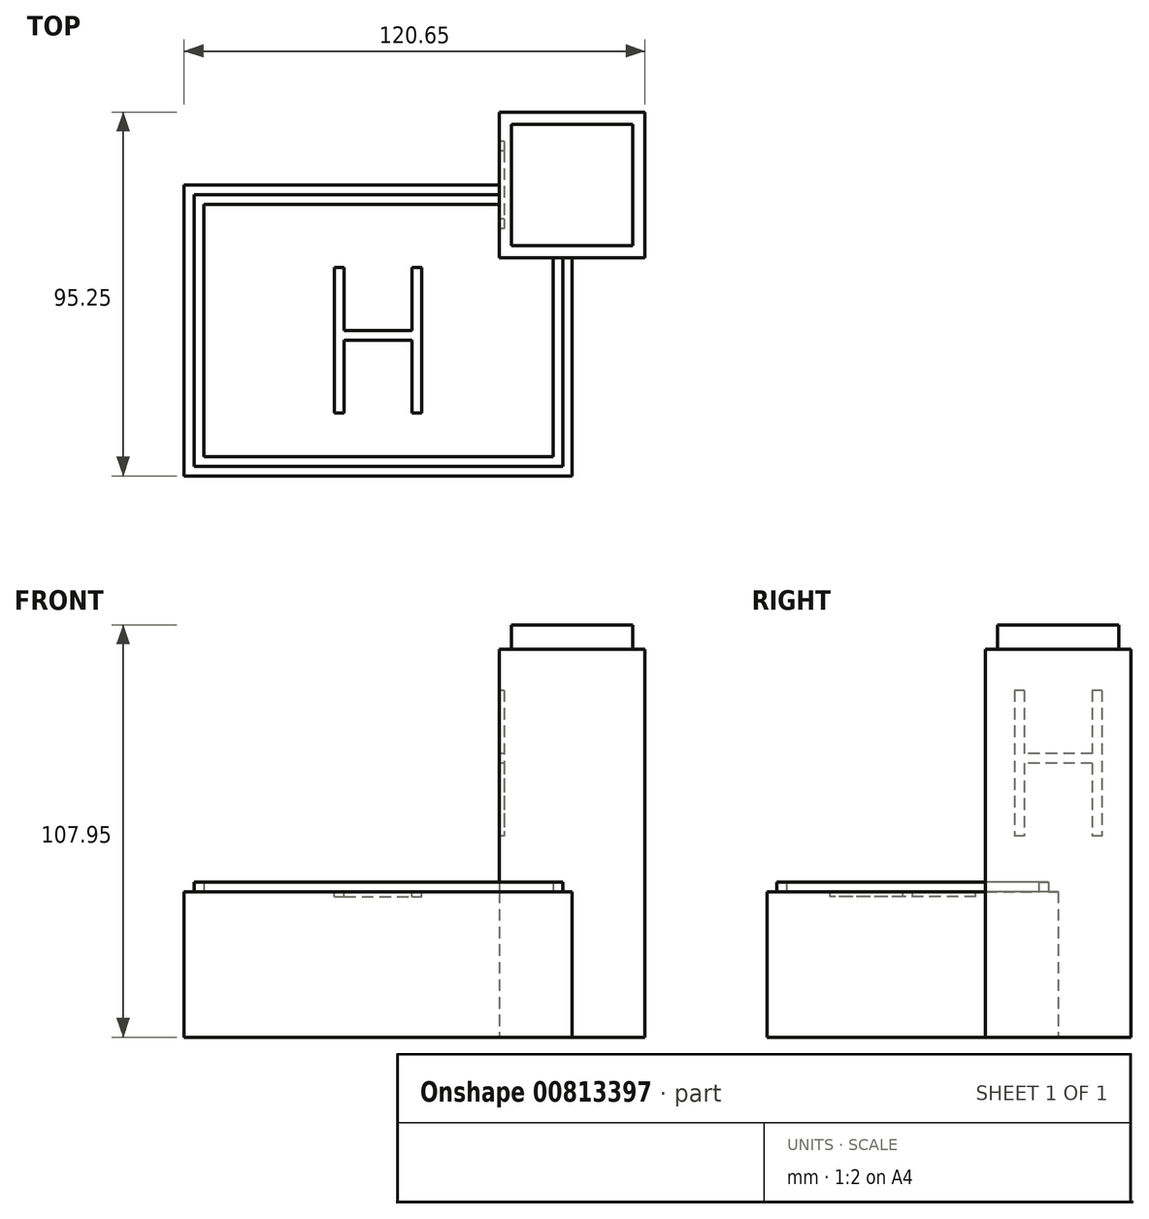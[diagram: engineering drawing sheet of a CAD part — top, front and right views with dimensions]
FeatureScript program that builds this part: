
annotation { "Feature Type Name" : "Feature", "Feature Type Description" : "" }
export const myFeature = defineFeature(function(context is Context, id is Id, definition is map)
    precondition{}
    {
        {
            var Q0;
            Q0=qCreatedBy(makeId("Top.planeOp"),FACE);
            var sketch = newSketch(context, id + "F0", { "sketchPlane" : qUnion([Q0])});
            skLineSegment(sketch, "E0.bottom", {"start": v(-50.8, 38.1) * mm, "end": v(50.8, 38.1) * mm});
            skLineSegment(sketch, "E0.top", {"start": v(-50.8, -38.1) * mm, "end": v(50.8, -38.1) * mm});
            skLineSegment(sketch, "E0.left", {"start": v(-50.8, 38.1) * mm, "end": v(-50.8, -38.1) * mm});
            skLineSegment(sketch, "E0.right", {"start": v(50.8, 38.1) * mm, "end": v(50.8, -38.1) * mm});
            skLineSegment(sketch, "E1.bottom", {"start": v(31.75, 57.15) * mm, "end": v(69.85, 57.15) * mm});
            skLineSegment(sketch, "E1.top", {"start": v(31.75, 19.05) * mm, "end": v(69.85, 19.05) * mm});
            skLineSegment(sketch, "E1.left", {"start": v(31.75, 57.15) * mm, "end": v(31.75, 19.05) * mm});
            skLineSegment(sketch, "E1.right", {"start": v(69.85, 57.15) * mm, "end": v(69.85, 19.05) * mm});
            skSolve(sketch);
        }
        {
            var Q0;
            {var subQ1=sQuery(id+"F0.wireOp",EDGE,"E0.top");Q0=makeQuery(id+"F0.imprint","IMPRINT",FACE,{"disambiguationData":[TD([[makeQuery(id+"F0.imprint","IMPRINT",EDGE,{"derivedFrom":subQ1}),1.0]])]});}
            var Q1;
            {var subQ0=sQuery(id+"F0.wireOp",EDGE,"E0.right");var subQ1=sQuery(id+"F0.wireOp",EDGE,"E0.bottom");var subQ2=makeQuery(id+"F0.imprint","INTERSECT",VERTEX,{"derivedFrom":[subQ1,subQ0]});Q1=makeQuery(id+"F0.imprint","IMPRINT",FACE,{"disambiguationData":[TD([[makeQuery(id+"F0.imprint","IMPRINT",EDGE,{"disambiguationData":[TD([[subQ2,1.0]])],"derivedFrom":subQ1}),-1.0]])]});}
            extrude(context, id + "F1", {"entities" : qUnion([Q0, Q1]), "depth" : 38.1 * mm, "offsetDistance" : 25.4 * mm});
        }
        {
            var Q0;
            {var subQ6=sQuery(id+"F0.wireOp",EDGE,"E1.bottom");Q0=makeQuery(id+"F0.imprint","IMPRINT",FACE,{"disambiguationData":[TD([[makeQuery(id+"F0.imprint","IMPRINT",EDGE,{"derivedFrom":subQ6}),-1.0]])]});}
            var Q1;
            {var subQ0=sQuery(id+"F0.wireOp",EDGE,"E0.right");var subQ1=sQuery(id+"F0.wireOp",EDGE,"E0.bottom");var subQ2=makeQuery(id+"F0.imprint","INTERSECT",VERTEX,{"derivedFrom":[subQ1,subQ0]});Q1=makeQuery(id+"F0.imprint","IMPRINT",FACE,{"disambiguationData":[TD([[makeQuery(id+"F0.imprint","IMPRINT",EDGE,{"disambiguationData":[TD([[subQ2,1.0]])],"derivedFrom":subQ1}),-1.0]])]});}
            extrude(context, id + "F2", {"entities" : qUnion([Q0, Q1]), "operationType" : NewBodyOperationType.ADD, "depth" : 101.6 * mm, "offsetDistance" : 25.4 * mm});
        }
        {
            var Q0;
            Q0=makeQuery(id+"F2.opExtrude","CAP_FACE",FACE,{"disambiguationData":[OSD([sQuery(id+"F0.wireOp",EDGE,"E1.bottom"),sQuery(id+"F0.wireOp",EDGE,"E1.top"),sQuery(id+"F0.wireOp",EDGE,"E1.left"),sQuery(id+"F0.wireOp",EDGE,"E1.right")])],"isStart":false});
            var sketch = newSketch(context, id + "F3", { "sketchPlane" : qUnion([Q0])});
            skLineSegment(sketch, "E2.bottom", {"start": v(34.93, 53.97) * mm, "end": v(66.68, 53.97) * mm});
            skLineSegment(sketch, "E2.top", {"start": v(34.93, 22.22) * mm, "end": v(66.68, 22.22) * mm});
            skLineSegment(sketch, "E2.left", {"start": v(34.93, 53.97) * mm, "end": v(34.93, 22.22) * mm});
            skLineSegment(sketch, "E2.right", {"start": v(66.68, 53.97) * mm, "end": v(66.68, 22.22) * mm});
            skSolve(sketch);
        }
        {
            var Q0;
            Q0=makeQuery(id+"F3.imprint","IMPRINT",FACE,{"disambiguationData":[TD([[makeQuery(id+"F3.imprint","IMPRINT",EDGE,{"derivedFrom":sQuery(id+"F3.wireOp",EDGE,"E2.bottom")}),-1.0]])]});
            extrude(context, id + "F4", {"entities" : qUnion([Q0]), "operationType" : NewBodyOperationType.ADD, "depth" : 6.35 * mm, "offsetDistance" : 25.4 * mm});
        }
        {
            var Q0;
            Q0=makeQuery(id+"F1.opExtrude","CAP_FACE",FACE,{"disambiguationData":[OSD([sQuery(id+"F0.wireOp",EDGE,"E0.bottom"),sQuery(id+"F0.wireOp",EDGE,"E0.top"),sQuery(id+"F0.wireOp",EDGE,"E0.left"),sQuery(id+"F0.wireOp",EDGE,"E0.right")])],"isStart":false});
            var sketch = newSketch(context, id + "F5", { "sketchPlane" : qUnion([Q0])});
            skLineSegment(sketch, "E3.bottom", {"start": v(-11.43, 16.51) * mm, "end": v(-8.9, 16.51) * mm});
            skLineSegment(sketch, "E3.top", {"start": v(-11.43, -21.59) * mm, "end": v(-8.9, -21.59) * mm});
            skLineSegment(sketch, "E3.left", {"start": v(-11.43, 16.51) * mm, "end": v(-11.43, -21.59) * mm});
            skLineSegment(sketch, "E3.right", {"start": v(-8.9, 16.51) * mm, "end": v(-8.9, -21.6) * mm});
            skLineSegment(sketch, "E4.bottom", {"start": v(8.89, 16.51) * mm, "end": v(11.43, 16.51) * mm});
            skLineSegment(sketch, "E4.top", {"start": v(8.89, -21.59) * mm, "end": v(11.43, -21.59) * mm});
            skLineSegment(sketch, "E4.left", {"start": v(8.89, 16.51) * mm, "end": v(8.89, -21.59) * mm});
            skLineSegment(sketch, "E4.right", {"start": v(11.43, 16.51) * mm, "end": v(11.43, -21.59) * mm});
            skLineSegment(sketch, "E5.bottom", {"start": v(-8.9, 0) * mm, "end": v(8.89, 0) * mm});
            skLineSegment(sketch, "E5.top", {"start": v(-8.9, -2.54) * mm, "end": v(8.89, -2.54) * mm});
            skLineSegment(sketch, "E5.left", {"start": v(-8.9, 0) * mm, "end": v(-8.9, -2.54) * mm});
            skLineSegment(sketch, "E5.right", {"start": v(8.89, 0) * mm, "end": v(8.89, -2.54) * mm});
            skPoint(sketch, "E6.centerSnap0", {"position": v(0, -2.54) * mm});
            skCircle(sketch, "E7", {"center": v(0, -2.54) * mm, "radius": 22.22 * mm});
            skCircle(sketch, "E8", {"center": v(0, -2.54) * mm, "radius": 23.42 * mm});
            skLineSegment(sketch, "E9", {"start": v(-23.42, -2.76) * mm, "end": v(-22.21, -2.76) * mm, "construction": true});
            skSolve(sketch);
        }
        {
            var Q0;
            Q0=makeQuery(id+"F5.imprint","IMPRINT",FACE,{"disambiguationData":[TD([[makeQuery(id+"F5.imprint","IMPRINT",EDGE,{"derivedFrom":sQuery(id+"F5.wireOp",EDGE,"E5.bottom")}),-1.0]])]});
            var Q1;
            {var subQ1=sQuery(id+"F5.wireOp",EDGE,"E3.bottom");Q1=makeQuery(id+"F5.imprint","IMPRINT",FACE,{"disambiguationData":[TD([[makeQuery(id+"F5.imprint","IMPRINT",EDGE,{"derivedFrom":subQ1}),-1.0]])]});}
            var Q2;
            {var subQ3=sQuery(id+"F5.wireOp",EDGE,"E4.bottom");Q2=makeQuery(id+"F5.imprint","IMPRINT",FACE,{"disambiguationData":[TD([[makeQuery(id+"F5.imprint","IMPRINT",EDGE,{"derivedFrom":subQ3}),-1.0]])]});}
            extrude(context, id + "F6", {"entities" : qUnion([Q0, Q1, Q2]), "operationType" : NewBodyOperationType.REMOVE, "oppositeDirection" : true, "depth" : 1.27 * mm, "offsetDistance" : 25.4 * mm});
        }
        {
            var Q0;
            Q0=makeQuery(id+"F1.opExtrude","CAP_FACE",FACE,{"disambiguationData":[OSD([sQuery(id+"F0.wireOp",EDGE,"E0.bottom"),sQuery(id+"F0.wireOp",EDGE,"E0.top"),sQuery(id+"F0.wireOp",EDGE,"E0.left"),sQuery(id+"F0.wireOp",EDGE,"E0.right")])],"isStart":false});
            var sketch = newSketch(context, id + "F7", { "sketchPlane" : qUnion([Q0])});
            skLineSegment(sketch, "E10.bottom", {"start": v(-48.2, 35.56) * mm, "end": v(-45.66, 35.56) * mm});
            skLineSegment(sketch, "E10.top", {"start": v(-48.2, -35.56) * mm, "end": v(-45.66, -35.56) * mm});
            skLineSegment(sketch, "E10.left", {"start": v(-48.2, 35.56) * mm, "end": v(-48.2, -35.56) * mm});
            skLineSegment(sketch, "E10.right", {"start": v(-45.66, 35.56) * mm, "end": v(-45.66, -35.56) * mm});
            skLineSegment(sketch, "E11.bottom", {"start": v(-45.66, -33.02) * mm, "end": v(48.32, -33.02) * mm});
            skLineSegment(sketch, "E11.top", {"start": v(-45.66, -35.56) * mm, "end": v(48.32, -35.56) * mm});
            skLineSegment(sketch, "E11.left", {"start": v(-45.66, -33.02) * mm, "end": v(-45.66, -35.56) * mm});
            skLineSegment(sketch, "E11.right", {"start": v(48.32, -33.02) * mm, "end": v(48.32, -35.56) * mm});
            skLineSegment(sketch, "E12.bottom", {"start": v(45.78, 19.05) * mm, "end": v(48.32, 19.05) * mm});
            skLineSegment(sketch, "E12.top", {"start": v(45.78, -33.02) * mm, "end": v(48.32, -33.02) * mm});
            skLineSegment(sketch, "E12.left", {"start": v(45.78, 19.05) * mm, "end": v(45.78, -33.02) * mm});
            skLineSegment(sketch, "E12.right", {"start": v(48.32, 19.05) * mm, "end": v(48.32, -33.02) * mm});
            skLineSegment(sketch, "E13.bottom", {"start": v(-45.66, 35.56) * mm, "end": v(31.75, 35.56) * mm});
            skLineSegment(sketch, "E13.top", {"start": v(-45.66, 33.02) * mm, "end": v(31.75, 33.02) * mm});
            skLineSegment(sketch, "E13.left", {"start": v(-45.66, 35.56) * mm, "end": v(-45.66, 33.02) * mm});
            skLineSegment(sketch, "E13.right", {"start": v(31.75, 35.56) * mm, "end": v(31.75, 33.02) * mm});
            skSolve(sketch);
        }
        {
            var Q0;
            Q0=makeQuery(id+"F7.imprint","IMPRINT",FACE,{"disambiguationData":[TD([[makeQuery(id+"F7.imprint","IMPRINT",EDGE,{"derivedFrom":sQuery(id+"F7.wireOp",EDGE,"E13.bottom")}),-1.0]])]});
            var Q1;
            Q1=makeQuery(id+"F7.imprint","IMPRINT",FACE,{"disambiguationData":[TD([[makeQuery(id+"F7.imprint","IMPRINT",EDGE,{"derivedFrom":sQuery(id+"F7.wireOp",EDGE,"E10.bottom")}),-1.0]])]});
            var Q2;
            Q2=makeQuery(id+"F7.imprint","IMPRINT",FACE,{"disambiguationData":[TD([[makeQuery(id+"F7.imprint","IMPRINT",EDGE,{"derivedFrom":sQuery(id+"F7.wireOp",EDGE,"E11.bottom")}),-1.0]])]});
            var Q3;
            Q3=makeQuery(id+"F7.imprint","IMPRINT",FACE,{"disambiguationData":[TD([[makeQuery(id+"F7.imprint","IMPRINT",EDGE,{"derivedFrom":sQuery(id+"F7.wireOp",EDGE,"E12.bottom")}),1.0]])]});
            extrude(context, id + "F8", {"entities" : qUnion([Q0, Q1, Q2, Q3]), "operationType" : NewBodyOperationType.ADD, "depth" : 2.54 * mm, "offsetDistance" : 25.4 * mm});
        }
        {
            var Q0;
            Q0=makeQuery(id+"F2.opExtrude","SWEPT_FACE",FACE,{"disambiguationData":[OSD([sQuery(id+"F0.wireOp",EDGE,"E1.left")])]});
            var sketch = newSketch(context, id + "F9", { "sketchPlane" : qUnion([Q0])});
            skLineSegment(sketch, "E14.bottom", {"start": v(-49.53, 90.78) * mm, "end": v(-46.99, 90.78) * mm});
            skLineSegment(sketch, "E14.top", {"start": v(-49.53, 52.68) * mm, "end": v(-46.99, 52.68) * mm});
            skLineSegment(sketch, "E14.left", {"start": v(-49.53, 90.78) * mm, "end": v(-49.53, 52.68) * mm});
            skLineSegment(sketch, "E14.right", {"start": v(-46.99, 90.78) * mm, "end": v(-46.99, 52.68) * mm});
            skLineSegment(sketch, "E15.bottom", {"start": v(-29.2, 90.78) * mm, "end": v(-26.67, 90.78) * mm});
            skLineSegment(sketch, "E15.top", {"start": v(-29.2, 52.68) * mm, "end": v(-26.67, 52.68) * mm});
            skLineSegment(sketch, "E15.left", {"start": v(-29.2, 90.78) * mm, "end": v(-29.2, 52.68) * mm});
            skLineSegment(sketch, "E15.right", {"start": v(-26.67, 90.78) * mm, "end": v(-26.67, 52.68) * mm});
            skLineSegment(sketch, "E16.bottom", {"start": v(-46.99, 74.27) * mm, "end": v(-29.2, 74.27) * mm});
            skLineSegment(sketch, "E16.top", {"start": v(-46.99, 71.73) * mm, "end": v(-29.2, 71.73) * mm});
            skLineSegment(sketch, "E16.left", {"start": v(-46.99, 74.27) * mm, "end": v(-46.99, 71.73) * mm});
            skLineSegment(sketch, "E16.right", {"start": v(-29.2, 74.27) * mm, "end": v(-29.2, 71.73) * mm});
            skSolve(sketch);
        }
        {
            var Q0;
            {var subQ1=sQuery(id+"F9.wireOp",EDGE,"E14.bottom");Q0=makeQuery(id+"F9.imprint","IMPRINT",FACE,{"disambiguationData":[TD([[makeQuery(id+"F9.imprint","IMPRINT",EDGE,{"derivedFrom":subQ1}),-1.0]])]});}
            var Q1;
            Q1=makeQuery(id+"F9.imprint","IMPRINT",FACE,{"disambiguationData":[TD([[makeQuery(id+"F9.imprint","IMPRINT",EDGE,{"derivedFrom":sQuery(id+"F9.wireOp",EDGE,"E16.bottom")}),-1.0]])]});
            var Q2;
            {var subQ3=sQuery(id+"F9.wireOp",EDGE,"E15.bottom");Q2=makeQuery(id+"F9.imprint","IMPRINT",FACE,{"disambiguationData":[TD([[makeQuery(id+"F9.imprint","IMPRINT",EDGE,{"derivedFrom":subQ3}),-1.0]])]});}
            extrude(context, id + "F10", {"entities" : qUnion([Q0, Q1, Q2]), "operationType" : NewBodyOperationType.REMOVE, "oppositeDirection" : true, "depth" : 1.27 * mm, "offsetDistance" : 25.4 * mm});
        }
    });
